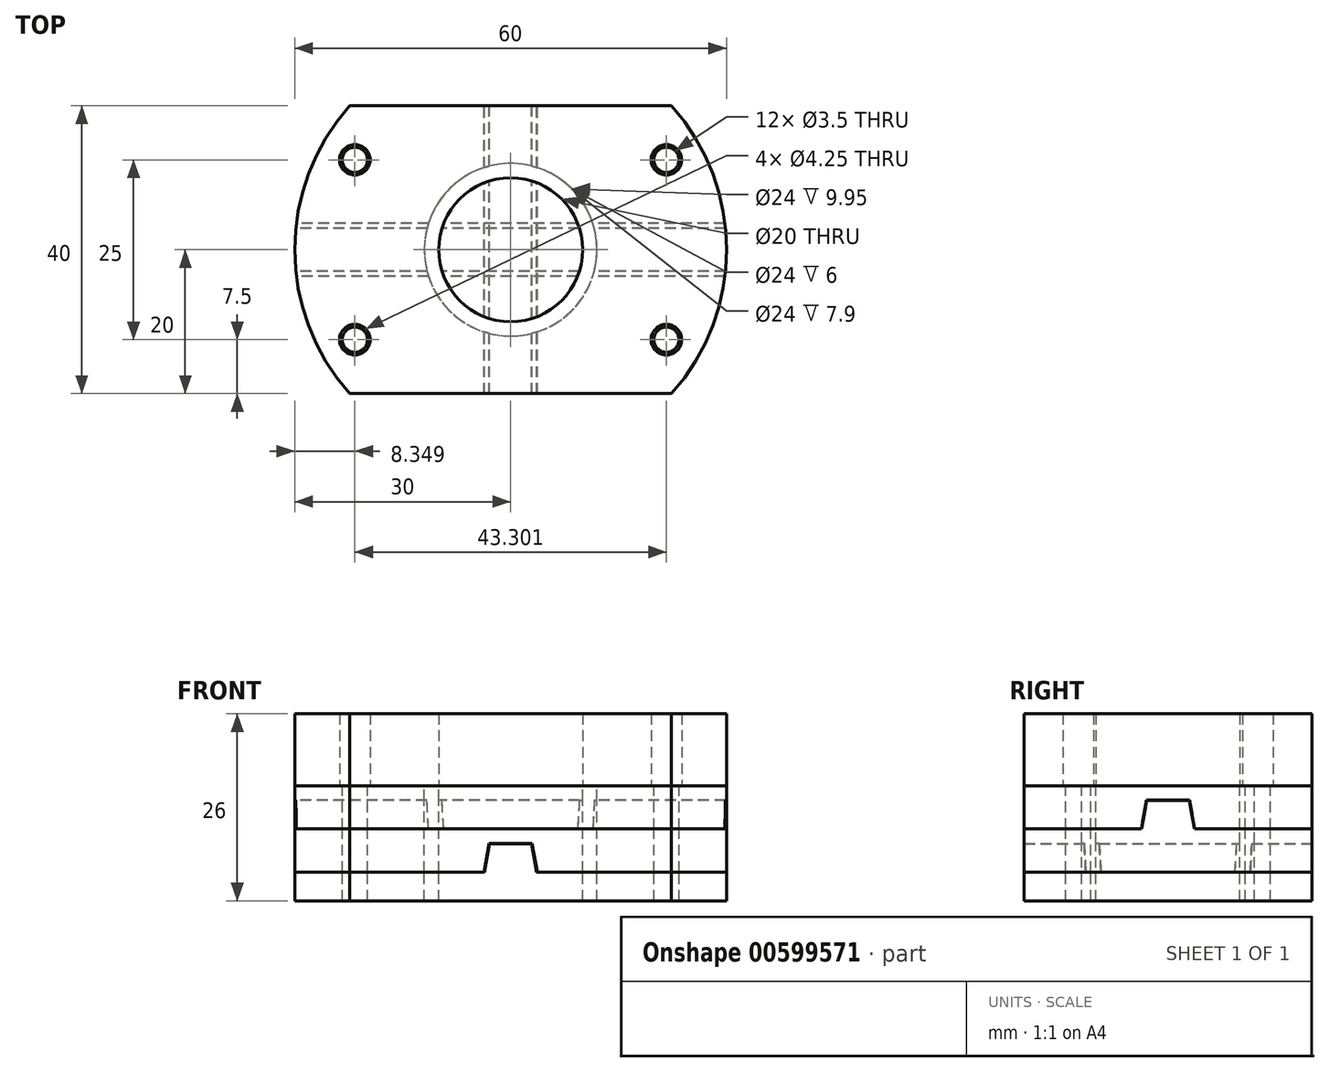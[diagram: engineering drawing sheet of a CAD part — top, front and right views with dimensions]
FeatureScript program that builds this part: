
annotation { "Feature Type Name" : "Feature", "Feature Type Description" : "" }
export const myFeature = defineFeature(function(context is Context, id is Id, definition is map)
    precondition{}
    {
        {
            var Q0;
            Q0=qCreatedBy(makeId("Top.planeOp"),FACE);
            var sketch = newSketch(context, id + "F0", { "sketchPlane" : qUnion([Q0])});
            skArc(sketch, "E0", {"start": v(-22.36, 20) * mm, "mid": v(-30, 0) * mm, "end": v(-22.36, -20) * mm});
            skLineSegment(sketch, "E1", {"start": v(-22.36, 20) * mm, "end": v(22.36, 20) * mm});
            skLineSegment(sketch, "E2", {"start": v(-22.36, -20) * mm, "end": v(22.36, -20) * mm});
            skLineSegment(sketch, "E3", {"start": v(0, 66.74) * mm, "end": v(0, -69.54) * mm, "construction": true});
            skArc(sketch, "E4.trimOffspring", {"start": v(22.36, -20) * mm, "mid": v(30, 0) * mm, "end": v(22.36, 20) * mm});
            skLineSegment(sketch, "E5", {"start": v(-52.5, 0) * mm, "end": v(45.2, 0) * mm, "construction": true});
            skCircle(sketch, "E6", {"center": v(0, 0) * mm, "radius": 25 * mm, "construction": true});
            skCircle(sketch, "E7", {"center": v(-21.65, 12.5) * mm, "radius": 2.12 * mm});
            skLineSegment(sketch, "E8", {"start": v(0, 0) * mm, "end": v(-21.65, 12.5) * mm, "construction": true});
            skCircle(sketch, "E9.MirrorC", {"center": v(-21.65, -12.5) * mm, "radius": 2.12 * mm});
            skCircle(sketch, "E10.MirrorC", {"center": v(21.65, 12.5) * mm, "radius": 2.12 * mm});
            skCircle(sketch, "E11.MirrorC", {"center": v(21.65, -12.5) * mm, "radius": 2.12 * mm});
            skCircle(sketch, "E12", {"center": v(0, 0) * mm, "radius": 10 * mm});
            skSolve(sketch);
        }
        {
            var Q0;
            Q0=makeQuery(id+"F0.imprint","IMPRINT",FACE,{"disambiguationData":[TD([[makeQuery(id+"F0.imprint","IMPRINT",EDGE,{"derivedFrom":sQuery(id+"F0.wireOp",EDGE,"E0")}),1.0]])]});
            extrude(context, id + "F1", {"entities" : qUnion([Q0]), "depth" : 10 * mm, "offsetDistance" : 25 * mm});
        }
        {
            var Q0;
            Q0=qCreatedBy(makeId("Right.planeOp"),FACE);
            var sketch = newSketch(context, id + "F2", { "sketchPlane" : qUnion([Q0])});
            skLineSegment(sketch, "E13.bottom", {"start": v(-20, 0) * mm, "end": v(20, 0) * mm});
            skLineSegment(sketch, "E13.top", {"start": v(-20, -6) * mm, "end": v(-3.7, -6) * mm});
            skLineSegment(sketch, "E13.left", {"start": v(-20, 0) * mm, "end": v(-20, -6) * mm});
            skLineSegment(sketch, "E13.right", {"start": v(20, 0) * mm, "end": v(20, -6) * mm});
            skLineSegment(sketch, "E14", {"start": v(-3.7, -6) * mm, "end": v(-3, -2) * mm});
            skLineSegment(sketch, "E15", {"start": v(-3, -2) * mm, "end": v(3, -2) * mm});
            skLineSegment(sketch, "E16", {"start": v(3, -2) * mm, "end": v(3.7, -6) * mm});
            skLineSegment(sketch, "E17", {"start": v(0, 11.55) * mm, "end": v(0, -15.7) * mm, "construction": true});
            skLineSegment(sketch, "E18.trimOffspring", {"start": v(3.7, -6) * mm, "end": v(20, -6) * mm});
            skSolve(sketch);
        }
        {
            var Q0;
            Q0=makeQuery(id+"F2.imprint","IMPRINT",FACE,{"disambiguationData":[TD([[makeQuery(id+"F2.imprint","IMPRINT",EDGE,{"derivedFrom":sQuery(id+"F2.wireOp",EDGE,"E13.bottom")}),-1.0]])]});
            extrude(context, id + "F3", {"entities" : qUnion([Q0]), "depth" : 50 * mm, "offsetDistance" : 25 * mm, "hasSecondDirection" : true, "secondDirectionOppositeDirection" : true, "secondDirectionDepth" : 50 * mm});
        }
        {
            var Q0;
            Q0=makeQuery(id+"F3.opExtrude","SWEPT_FACE",FACE,{"disambiguationData":[OSD([sQuery(id+"F2.wireOp",EDGE,"E13.bottom")])]});
            var sketch = newSketch(context, id + "F4", { "sketchPlane" : qUnion([Q0])});
            skArc(sketch, "E19.0", {"start": v(22.36, -20) * mm, "mid": v(30, 0) * mm, "end": v(22.36, 20) * mm});
            skArc(sketch, "E20.0", {"start": v(-22.36, 20) * mm, "mid": v(-30, 0) * mm, "end": v(-22.36, -20) * mm});
            skLineSegment(sketch, "E21.0", {"start": v(50, -20) * mm, "end": v(22.36, -20) * mm});
            skLineSegment(sketch, "E22.0", {"start": v(-50, -20) * mm, "end": v(-50, 20) * mm});
            skLineSegment(sketch, "E23.0", {"start": v(50, 20) * mm, "end": v(22.36, 20) * mm});
            skLineSegment(sketch, "E24.0", {"start": v(50, -20) * mm, "end": v(50, 20) * mm});
            skCircle(sketch, "E25.0", {"center": v(0, 0) * mm, "radius": 10 * mm});
            skLineSegment(sketch, "E26.trimOffspring", {"start": v(-22.36, -20) * mm, "end": v(-50, -20) * mm});
            skLineSegment(sketch, "E27.trimOffspring", {"start": v(-22.36, 20) * mm, "end": v(-50, 20) * mm});
            skCircle(sketch, "E28.0", {"center": v(0, 0) * mm, "radius": 12 * mm});
            skSolve(sketch);
        }
        {
            var Q0;
            Q0=qCreatedBy(makeId("Right.planeOp"),FACE);
            var sketch = newSketch(context, id + "F5", { "sketchPlane" : qUnion([Q0])});
            skLineSegment(sketch, "E29.bottom", {"start": v(-20, -6) * mm, "end": v(-3.65, -6) * mm});
            skLineSegment(sketch, "E29.top", {"start": v(-20, -12) * mm, "end": v(20, -12) * mm});
            skLineSegment(sketch, "E29.left", {"start": v(-20, -6) * mm, "end": v(-20, -12) * mm});
            skLineSegment(sketch, "E29.right", {"start": v(20, -6) * mm, "end": v(20, -12) * mm});
            skLineSegment(sketch, "E30.0", {"start": v(2.96, -2.05) * mm, "end": v(3.65, -6) * mm});
            skLineSegment(sketch, "E30.1", {"start": v(-2.96, -2.05) * mm, "end": v(2.96, -2.05) * mm});
            skLineSegment(sketch, "E30.2", {"start": v(-3.65, -6) * mm, "end": v(-2.96, -2.05) * mm});
            skLineSegment(sketch, "E31.trimOffspring", {"start": v(3.65, -6) * mm, "end": v(20, -6) * mm});
            skSolve(sketch);
        }
        {
            var Q0;
            Q0=makeQuery(id+"F5.imprint","IMPRINT",FACE,{"disambiguationData":[TD([[makeQuery(id+"F5.imprint","IMPRINT",EDGE,{"derivedFrom":sQuery(id+"F5.wireOp",EDGE,"E29.bottom")}),-1.0]])]});
            extrude(context, id + "F6", {"entities" : qUnion([Q0]), "depth" : 50 * mm, "offsetDistance" : 25 * mm, "hasSecondDirection" : true, "secondDirectionOppositeDirection" : true, "secondDirectionDepth" : 50 * mm});
        }
        {
            var Q0;
            Q0=makeQuery(id+"F6.opExtrude","SWEPT_FACE",FACE,{"disambiguationData":[OSD([sQuery(id+"F5.wireOp",EDGE,"E29.right")])]});
            var sketch = newSketch(context, id + "F7", { "sketchPlane" : qUnion([Q0])});
            skLineSegment(sketch, "E32", {"start": v(-3.7, -12) * mm, "end": v(-3, -8) * mm});
            skLineSegment(sketch, "E33", {"start": v(-3, -8) * mm, "end": v(3, -8) * mm});
            skLineSegment(sketch, "E34", {"start": v(3, -8) * mm, "end": v(3.7, -12) * mm});
            skLineSegment(sketch, "E35", {"start": v(3.7, -12) * mm, "end": v(-3.7, -12) * mm});
            skLineSegment(sketch, "E36", {"start": v(0, -4.65) * mm, "end": v(0, -15.84) * mm, "construction": true});
            skPoint(sketch, "E36.startSnap0", {"position": v(0, -6) * mm});
            skSolve(sketch);
        }
        {
            var Q0;
            Q0=makeQuery(id+"F7.imprint","IMPRINT",FACE,{"disambiguationData":[TD([[makeQuery(id+"F7.imprint","IMPRINT",EDGE,{"derivedFrom":sQuery(id+"F7.wireOp",EDGE,"E32")}),-1.0]])]});
            extrude(context, id + "F8", {"entities" : qUnion([Q0]), "operationType" : NewBodyOperationType.REMOVE, "endBound" : BoundingType.THROUGH_ALL, "oppositeDirection" : true, "depth" : 25 * mm, "offsetDistance" : 25 * mm});
        }
        {
            var Q0;
            Q0=makeQuery(id+"F6.opExtrude","SWEPT_FACE",FACE,{"disambiguationData":[OSD([sQuery(id+"F5.wireOp",EDGE,"E29.right")])]});
            var sketch = newSketch(context, id + "F9", { "sketchPlane" : qUnion([Q0])});
            skLineSegment(sketch, "E37", {"start": v(-36.52, -12) * mm, "end": v(-3.6, -12) * mm});
            skLineSegment(sketch, "E38", {"start": v(37.25, -12) * mm, "end": v(37.25, -16) * mm});
            skLineSegment(sketch, "E39", {"start": v(37.25, -16) * mm, "end": v(-36.52, -16) * mm});
            skLineSegment(sketch, "E40", {"start": v(-36.52, -16) * mm, "end": v(-36.52, -12) * mm});
            skLineSegment(sketch, "E41.0", {"start": v(2.92, -8.1) * mm, "end": v(3.6, -12) * mm});
            skLineSegment(sketch, "E41.1", {"start": v(-2.92, -8.1) * mm, "end": v(2.92, -8.1) * mm});
            skLineSegment(sketch, "E41.2", {"start": v(-3.6, -12) * mm, "end": v(-2.92, -8.1) * mm});
            skLineSegment(sketch, "E42.trimOffspring", {"start": v(3.6, -12) * mm, "end": v(37.25, -12) * mm});
            skSolve(sketch);
        }
        {
            var Q0;
            {var subQ12=sQuery(id+"F9.wireOp",EDGE,"E38");Q0=makeQuery(id+"F9.imprint","IMPRINT",FACE,{"disambiguationData":[TD([[makeQuery(id+"F9.imprint","IMPRINT",EDGE,{"derivedFrom":subQ12}),-1.0]])]});}
            extrude(context, id + "F10", {"entities" : qUnion([Q0]), "oppositeDirection" : true, "depth" : 40 * mm, "offsetDistance" : 25 * mm});
        }
        {
            var Q0;
            Q0 = qSketchRegion(id + "F4", true);
            extrude(context, id + "F11", {"entities" : qUnion([Q0]), "operationType" : NewBodyOperationType.REMOVE, "oppositeDirection" : true, "depth" : 25 * mm, "offsetDistance" : 25 * mm});
        }
        {
            var Q0;
            Q0=makeQuery(id+"F1.opExtrude","CAP_FACE",FACE,{"disambiguationData":[OSD([sQuery(id+"F0.wireOp",EDGE,"E0"),sQuery(id+"F0.wireOp",EDGE,"E1"),sQuery(id+"F0.wireOp",EDGE,"E2"),sQuery(id+"F0.wireOp",EDGE,"E4.trimOffspring"),sQuery(id+"F0.wireOp",EDGE,"E7"),sQuery(id+"F0.wireOp",EDGE,"E9.MirrorC"),sQuery(id+"F0.wireOp",EDGE,"E10.MirrorC"),sQuery(id+"F0.wireOp",EDGE,"E11.MirrorC"),sQuery(id+"F0.wireOp",EDGE,"E12")])],"isStart":false});
            var sketch = newSketch(context, id + "F12", { "sketchPlane" : qUnion([Q0])});
            skCircle(sketch, "E43", {"center": v(21.65, -12.5) * mm, "radius": 1.75 * mm});
            skLineSegment(sketch, "E44", {"start": v(36.83, 0) * mm, "end": v(-38.76, 0) * mm, "construction": true});
            skLineSegment(sketch, "E45", {"start": v(0, -36.26) * mm, "end": v(0, 16.04) * mm, "construction": true});
            skCircle(sketch, "E46.MirrorC", {"center": v(21.65, 12.5) * mm, "radius": 1.75 * mm});
            skCircle(sketch, "E47.MirrorC", {"center": v(-21.65, -12.5) * mm, "radius": 1.75 * mm});
            skCircle(sketch, "E48.MirrorC", {"center": v(-21.65, 12.5) * mm, "radius": 1.75 * mm});
            skSolve(sketch);
        }
        {
            var Q0;
            Q0 = qSketchRegion(id + "F12", true);
            extrude(context, id + "F13", {"entities" : qUnion([Q0]), "operationType" : NewBodyOperationType.REMOVE, "oppositeDirection" : true, "depth" : 50 * mm, "offsetDistance" : 25 * mm});
        }
    });
